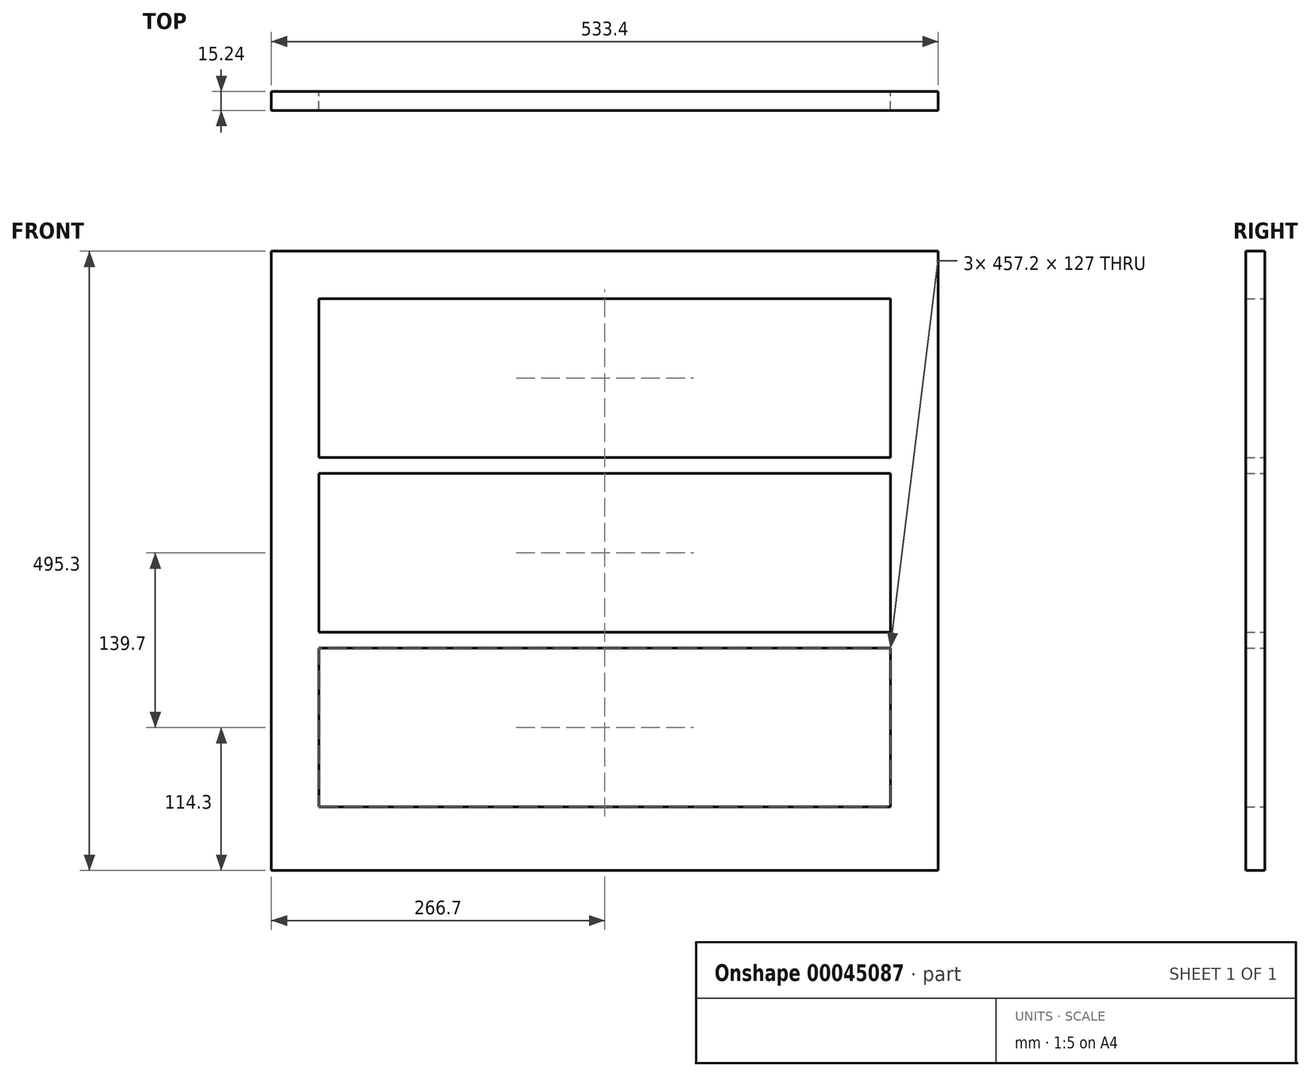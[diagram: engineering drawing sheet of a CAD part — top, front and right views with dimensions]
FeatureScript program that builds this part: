
annotation { "Feature Type Name" : "Feature", "Feature Type Description" : "" }
export const myFeature = defineFeature(function(context is Context, id is Id, definition is map)
    precondition{}
    {
        {
            var Q0;
            Q0=qCreatedBy(makeId("Front.planeOp"),FACE);
            var sketch = newSketch(context, id + "F0", { "sketchPlane" : qUnion([Q0])});
            skLineSegment(sketch, "E0.rect.bottom", {"start": v(-266.7, 247.65) * mm, "end": v(266.7, 247.65) * mm});
            skLineSegment(sketch, "E0.rect.top", {"start": v(-266.7, -247.65) * mm, "end": v(266.7, -247.65) * mm});
            skLineSegment(sketch, "E0.rect.left", {"start": v(-266.7, 247.65) * mm, "end": v(-266.7, -247.65) * mm});
            skLineSegment(sketch, "E0.rect.right", {"start": v(266.7, 247.65) * mm, "end": v(266.7, -247.65) * mm});
            skPoint(sketch, "E0.rect.middle", {"position": v(0, 0) * mm});
            skLineSegment(sketch, "E1.bottom", {"start": v(-228.6, 209.55) * mm, "end": v(228.6, 209.55) * mm});
            skLineSegment(sketch, "E1.top", {"start": v(-228.6, 82.55) * mm, "end": v(228.6, 82.55) * mm});
            skLineSegment(sketch, "E1.left", {"start": v(-228.6, 209.55) * mm, "end": v(-228.6, 82.55) * mm});
            skLineSegment(sketch, "E1.right", {"start": v(228.6, 209.55) * mm, "end": v(228.6, 82.55) * mm});
            skLineSegment(sketch, "E2", {"start": v(0, 82.55) * mm, "end": v(0, 209.55) * mm, "construction": true});
            skLineSegment(sketch, "E3.0.1.0", {"start": v(-228.6, 69.85) * mm, "end": v(-228.6, -57.15) * mm});
            skLineSegment(sketch, "E3.0.1.1", {"start": v(-228.6, 69.85) * mm, "end": v(228.6, 69.85) * mm});
            skLineSegment(sketch, "E3.0.1.2", {"start": v(228.6, 69.85) * mm, "end": v(228.6, -57.15) * mm});
            skLineSegment(sketch, "E3.0.1.3", {"start": v(-228.6, -57.15) * mm, "end": v(228.6, -57.15) * mm});
            skLineSegment(sketch, "E3.0.2.0", {"start": v(-228.6, -69.85) * mm, "end": v(-228.6, -196.85) * mm});
            skLineSegment(sketch, "E3.0.2.1", {"start": v(-228.6, -69.85) * mm, "end": v(228.6, -69.85) * mm});
            skLineSegment(sketch, "E3.0.2.2", {"start": v(228.6, -69.85) * mm, "end": v(228.6, -196.85) * mm});
            skLineSegment(sketch, "E3.0.2.3", {"start": v(-228.6, -196.85) * mm, "end": v(228.6, -196.85) * mm});
            skLineSegment(sketch, "E3.direction1", {"start": v(-228.6, 82.55) * mm, "end": v(-203.2, 82.55) * mm, "construction": true});
            skLineSegment(sketch, "E3.direction2", {"start": v(-228.6, 82.55) * mm, "end": v(-228.6, -57.15) * mm, "construction": true});
            skSolve(sketch);
        }
        {
            var Q0;
            Q0 = qSketchRegion(id + "F0", true);
            extrude(context, id + "F1", {"entities" : qUnion([Q0]), "depth" : 15.24 * mm});
        }
    });
